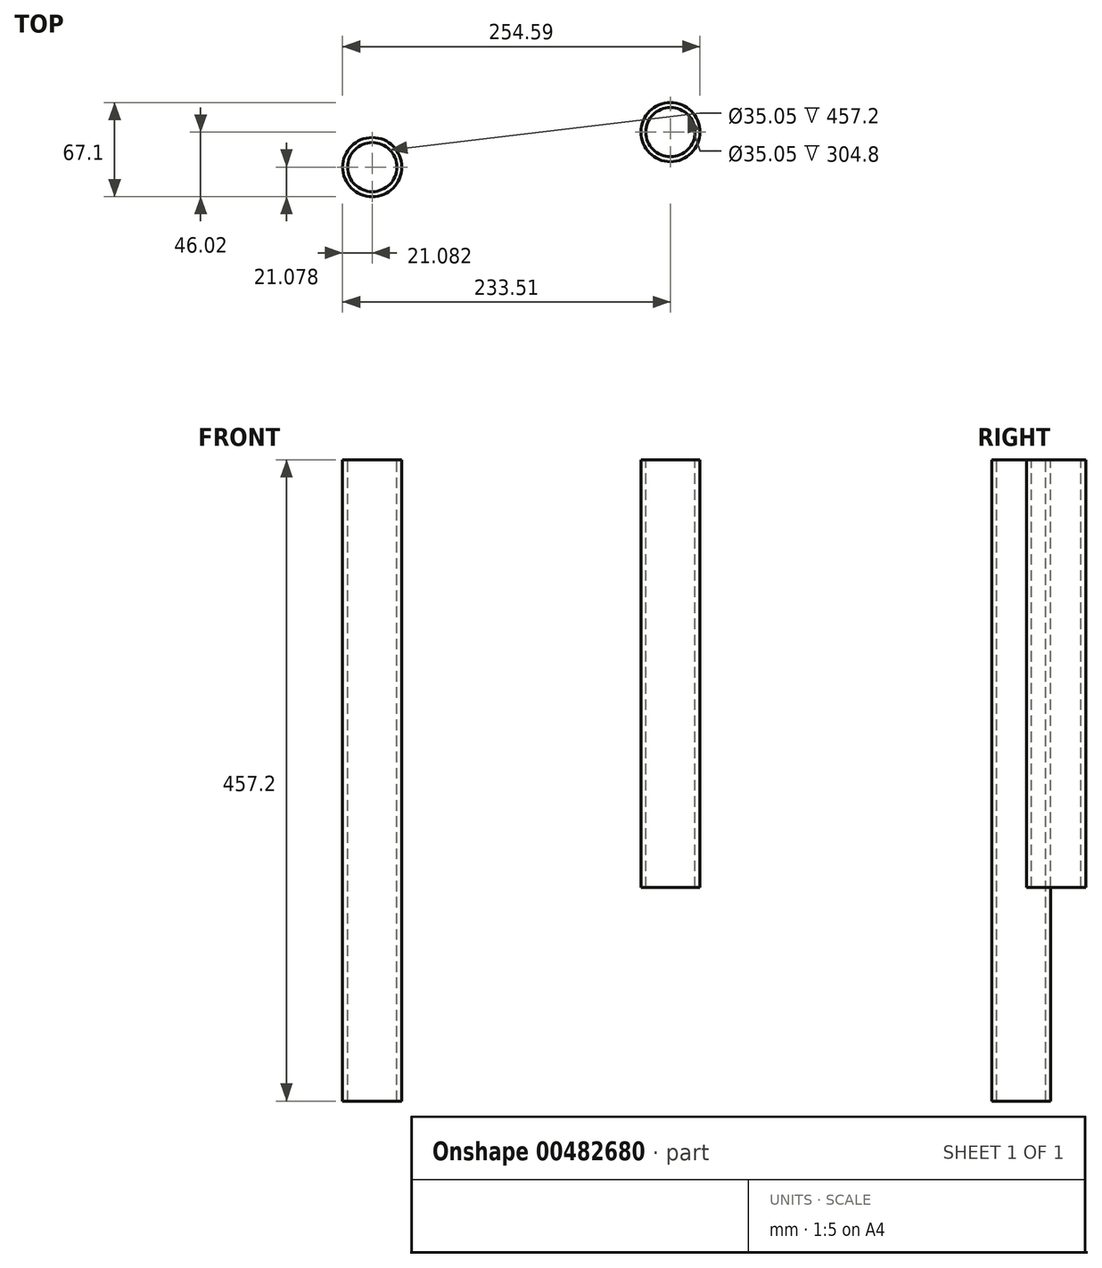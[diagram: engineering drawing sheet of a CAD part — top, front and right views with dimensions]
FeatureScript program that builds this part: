
annotation { "Feature Type Name" : "Feature", "Feature Type Description" : "" }
export const myFeature = defineFeature(function(context is Context, id is Id, definition is map)
    precondition{}
    {
        {
            var Q0;
            Q0=qCreatedBy(makeId("Top.planeOp"),FACE);
            var sketch = newSketch(context, id + "F0", { "sketchPlane" : qUnion([Q0])});
            skCircle(sketch, "E0", {"center": v(0, 0) * mm, "radius": 21.08 * mm});
            skCircle(sketch, "E1", {"center": v(0, 0) * mm, "radius": 17.53 * mm});
            skSolve(sketch);
        }
        {
            var Q0;
            Q0 = qSketchRegion(id + "F0", true);
            extrude(context, id + "F1", {"entities" : qUnion([Q0]), "oppositeDirection" : true, "depth" : 304.8 * mm});
        }
        {
            var Q0;
            Q0=qCreatedBy(makeId("Top.planeOp"),FACE);
            var sketch = newSketch(context, id + "F2", { "sketchPlane" : qUnion([Q0])});
            skCircle(sketch, "E2", {"center": v(-212.43, -24.94) * mm, "radius": 21.08 * mm});
            skCircle(sketch, "E3", {"center": v(-212.43, -24.94) * mm, "radius": 17.53 * mm});
            skSolve(sketch);
        }
        {
            var Q0;
            Q0 = qSketchRegion(id + "F2", true);
            extrude(context, id + "F3", {"entities" : qUnion([Q0]), "oppositeDirection" : true, "depth" : 457.2 * mm});
        }
    });
